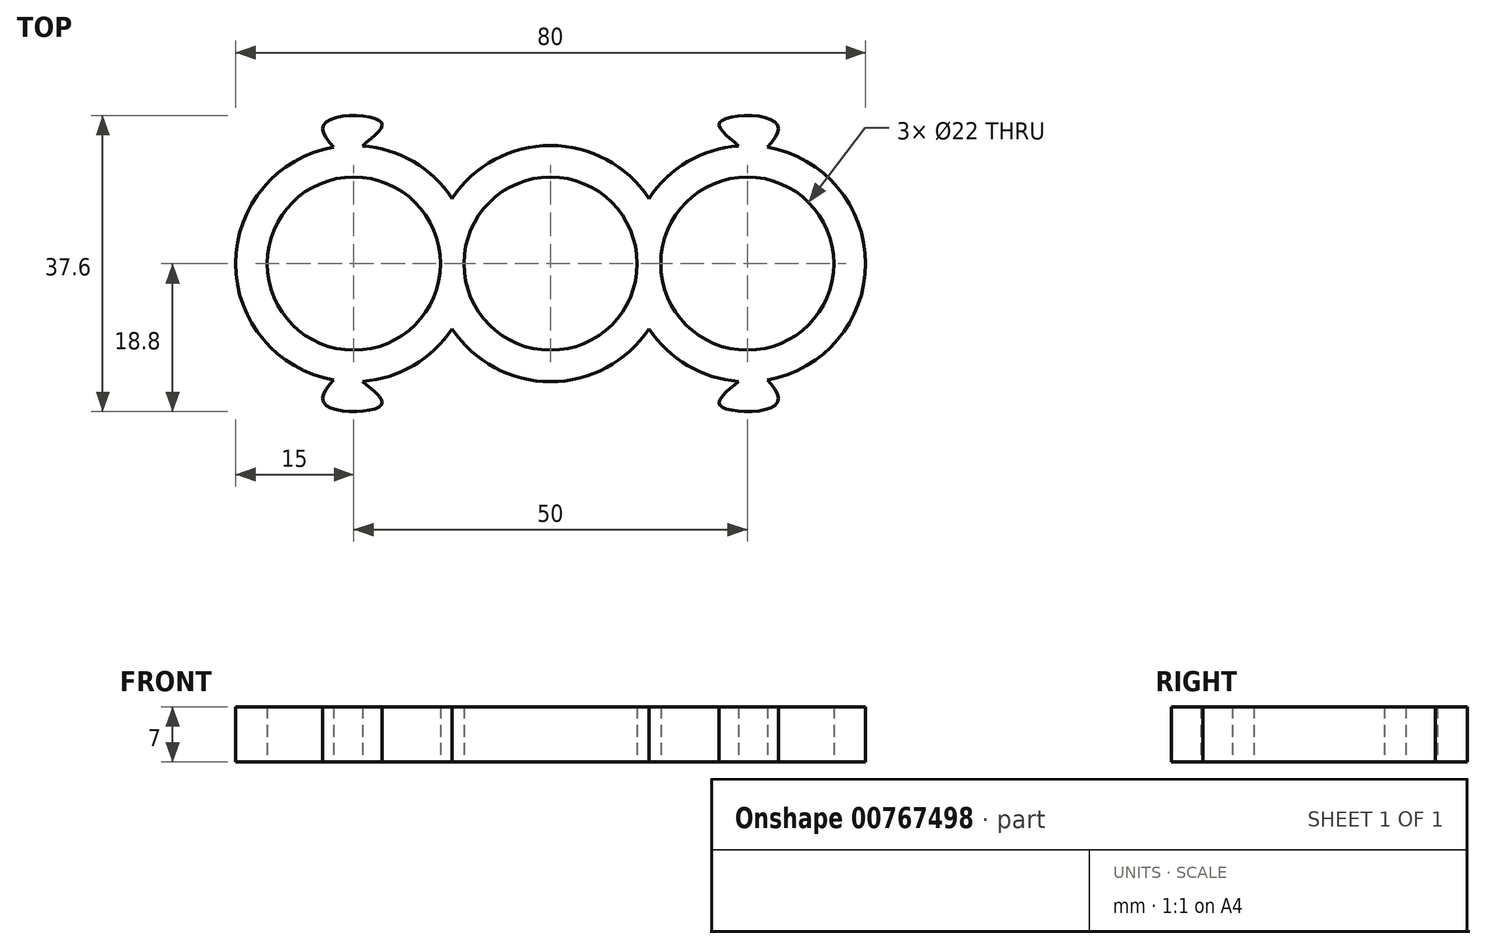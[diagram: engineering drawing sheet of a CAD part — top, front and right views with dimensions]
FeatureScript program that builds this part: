
annotation { "Feature Type Name" : "Feature", "Feature Type Description" : "" }
export const myFeature = defineFeature(function(context is Context, id is Id, definition is map)
    precondition{}
    {
        {
            var Q0;
            Q0=qCreatedBy(makeId("Top.planeOp"),FACE);
            var sketch = newSketch(context, id + "F0", { "sketchPlane" : qUnion([Q0])});
            skArc(sketch, "E0", {"start": v(0, 11) * mm, "mid": v(-11, 0) * mm, "end": v(0, -11) * mm});
            skArc(sketch, "E1", {"start": v(-12.5, -8.3) * mm, "mid": v(-7.1, -13.22) * mm, "end": v(0, -15) * mm});
            skCircle(sketch, "E2", {"center": v(-25, 0) * mm, "radius": 11 * mm});
            skArc(sketch, "E3.trimOffspring", {"start": v(-12.5, 8.3) * mm, "mid": v(-17.42, 12.94) * mm, "end": v(-23.88, 14.96) * mm});
            skArc(sketch, "E4.trimOffspring", {"start": v(0, 15) * mm, "mid": v(-7.1, 13.22) * mm, "end": v(-12.5, 8.3) * mm});
            skArc(sketch, "E5.MirrorCS", {"start": v(12.5, 8.3) * mm, "mid": v(17.42, 12.94) * mm, "end": v(23.88, 14.96) * mm});
            skCircle(sketch, "E6.MirrorC", {"center": v(25, 0) * mm, "radius": 11 * mm});
            skArc(sketch, "E7.MirrorCS", {"start": v(0, 15) * mm, "mid": v(7.1, 13.22) * mm, "end": v(12.5, 8.3) * mm});
            skArc(sketch, "E8.MirrorCS", {"start": v(12.5, -8.3) * mm, "mid": v(7.1, -13.22) * mm, "end": v(0, -15) * mm});
            skArc(sketch, "E9.MirrorCS", {"start": v(0, 11) * mm, "mid": v(11, 0) * mm, "end": v(0, -11) * mm});
            skFitSpline(sketch, "E10", {"points": [v(-25.08, -12.9) * mm, v(-28.86, -17.55) * mm, v(-21.47, -17.9) * mm, v(-24.74, -13.94) * mm, v(-25.08, -12.9) * mm]});
            skArc(sketch, "E11.trimOffspring", {"start": v(-23.88, -14.96) * mm, "mid": v(-17.42, -12.94) * mm, "end": v(-12.5, -8.3) * mm});
            skFitSpline(sketch, "E12.MirrorCS", {"points": [v(-25.08, 12.9) * mm, v(-28.86, 17.55) * mm, v(-21.47, 17.9) * mm, v(-24.74, 13.94) * mm, v(-25.08, 12.9) * mm]});
            skFitSpline(sketch, "E13.MirrorCS", {"points": [v(25.08, 12.9) * mm, v(28.86, 17.55) * mm, v(21.47, 17.9) * mm, v(24.74, 13.94) * mm, v(25.08, 12.9) * mm]});
            skFitSpline(sketch, "E14.MirrorCS", {"points": [v(25.08, -12.9) * mm, v(28.86, -17.55) * mm, v(21.47, -17.9) * mm, v(24.74, -13.94) * mm, v(25.08, -12.9) * mm]});
            skArc(sketch, "E15.trimOffspring", {"start": v(-27.55, 14.78) * mm, "mid": v(-40, 0) * mm, "end": v(-27.55, -14.78) * mm});
            skArc(sketch, "E16.trimOffspring", {"start": v(27.55, 14.78) * mm, "mid": v(40, 0) * mm, "end": v(27.55, -14.78) * mm});
            skArc(sketch, "E17.trimOffspring", {"start": v(23.88, -14.96) * mm, "mid": v(17.42, -12.94) * mm, "end": v(12.5, -8.3) * mm});
            skSolve(sketch);
        }
        {
            var Q0;
            Q0=qSketchRegion(id+"F0",true);
            extrude(context, id + "F1", {"entities" : qUnion([Q0]), "depth" : 7 * mm, "offsetDistance" : 25 * mm});
        }
    });
